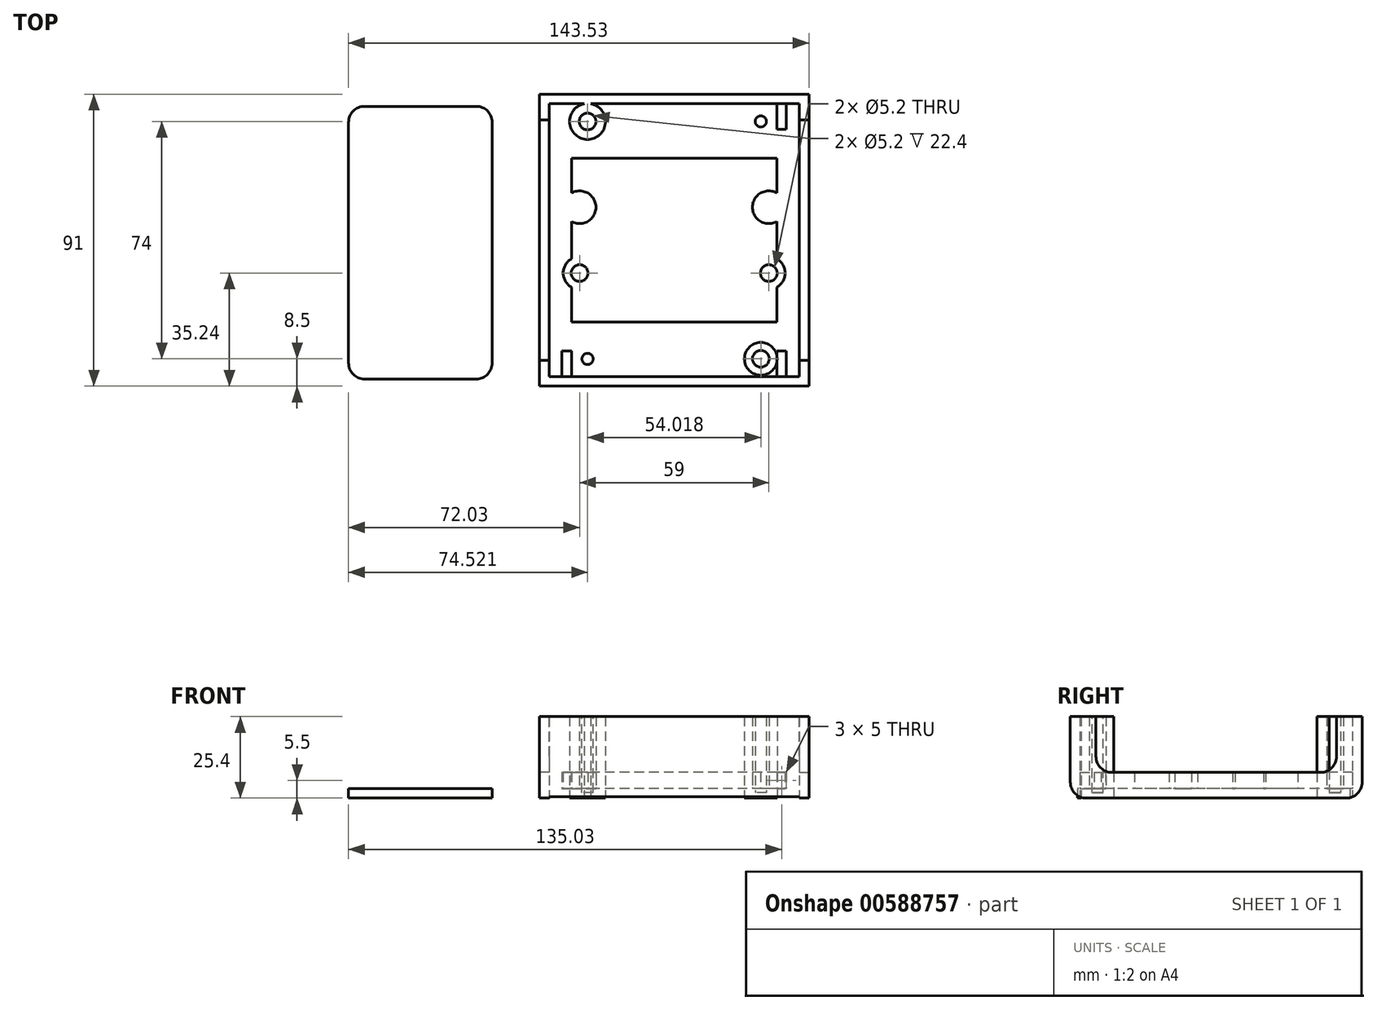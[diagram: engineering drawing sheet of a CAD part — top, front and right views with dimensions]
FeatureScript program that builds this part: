
annotation { "Feature Type Name" : "Feature", "Feature Type Description" : "" }
export const myFeature = defineFeature(function(context is Context, id is Id, definition is map)
    precondition{}
    {
        {
            assignVariable(context, id + "F0", {"name" : "hull_thickness", "anyValue" : 3});
        }
        {
            assignVariable(context, id + "F1", {"name" : "height", "anyValue" : 25.4});
        }
        {
            var Q0;
            Q0=qCreatedBy(makeId("Top.planeOp"),FACE);
            var sketch = newSketch(context, id + "F2", { "sketchPlane" : qUnion([Q0])});
            skLineSegment(sketch, "E0.bottom", {"start": v(42, 45.5) * mm, "end": v(-42, 45.5) * mm});
            skLineSegment(sketch, "E0.top", {"start": v(42, -45.5) * mm, "end": v(-42, -45.5) * mm});
            skLineSegment(sketch, "E0.left", {"start": v(42, 45.5) * mm, "end": v(42, -45.5) * mm});
            skLineSegment(sketch, "E0.right", {"start": v(-42, 45.5) * mm, "end": v(-42, -45.5) * mm});
            skPoint(sketch, "E0.middle", {"position": v(0, 0) * mm});
            skSolve(sketch);
        }
        {
            var Q0;
            Q0=makeQuery(id+"F2.imprint","IMPRINT",FACE,{"disambiguationData":[TD([[makeQuery(id+"F2.imprint","IMPRINT",EDGE,{"derivedFrom":sQuery(id+"F2.wireOp",EDGE,"E0.bottom")}),1.0]])]});
            extrude(context, id + "F3", {"entities" : qUnion([Q0]), "depth" : (getVariable(context, 'height')) * mm, "offsetDistance" : 25 * mm});
        }
        {
            var Q0;
            Q0=makeQuery(id+"F3.opExtrude","CAP_FACE",FACE,{"disambiguationData":[OSD([sQuery(id+"F2.wireOp",EDGE,"E0.bottom"),sQuery(id+"F2.wireOp",EDGE,"E0.top"),sQuery(id+"F2.wireOp",EDGE,"E0.left"),sQuery(id+"F2.wireOp",EDGE,"E0.right")])],"isStart":false});
            shell(context, id + "F4", {"entities" : qUnion([Q0]), "thickness" : (getVariable(context, 'hull_thickness')) * mm});
        }
        {
            var Q0;
            Q0=makeQuery(id+"F4.opShell","OFFSET_FACE",FACE,{"disambiguationData":[OSD([sQuery(id+"F2.wireOp",EDGE,"E0.bottom"),sQuery(id+"F2.wireOp",EDGE,"E0.top"),sQuery(id+"F2.wireOp",EDGE,"E0.left"),sQuery(id+"F2.wireOp",EDGE,"E0.right")])]});
            var sketch = newSketch(context, id + "F5", { "sketchPlane" : qUnion([Q0])});
            skLineSegment(sketch, "E1.bottom", {"start": v(42, 45.5) * mm, "end": v(-42, 45.5) * mm});
            skLineSegment(sketch, "E1.top", {"start": v(42, -45.5) * mm, "end": v(-42, -45.5) * mm});
            skLineSegment(sketch, "E1.left", {"start": v(42, 45.5) * mm, "end": v(42, -45.5) * mm});
            skLineSegment(sketch, "E1.right", {"start": v(-42, 45.5) * mm, "end": v(-42, -45.5) * mm});
            skPoint(sketch, "E1.middle", {"position": v(0, 0) * mm});
            skCircle(sketch, "E2", {"center": v(-27, 37) * mm, "radius": 2.6 * mm});
            skCircle(sketch, "E3.MirrorC", {"center": v(27, -37) * mm, "radius": 2.6 * mm});
            skCircle(sketch, "E4.MirrorC", {"center": v(27, 37) * mm, "radius": 1.75 * mm});
            skCircle(sketch, "E5.MirrorC", {"center": v(-27, -37) * mm, "radius": 1.75 * mm});
            skCircle(sketch, "E6", {"center": v(-27, 37) * mm, "radius": 5.6 * mm});
            skCircle(sketch, "E7", {"center": v(27, 37) * mm, "radius": 5.1 * mm});
            skCircle(sketch, "E8", {"center": v(27, -37) * mm, "radius": 5.1 * mm});
            skCircle(sketch, "E9", {"center": v(-27, -37) * mm, "radius": 5.1 * mm});
            skSolve(sketch);
        }
        {
            var Q0;
            Q0=makeQuery(id+"F5.imprint","IMPRINT",FACE,{"disambiguationData":[TD([[makeQuery(id+"F5.imprint","IMPRINT",EDGE,{"derivedFrom":sQuery(id+"F5.wireOp",EDGE,"E2")}),-1.0]])]});
            var Q1;
            Q1=makeQuery(id+"F5.imprint","IMPRINT",FACE,{"disambiguationData":[TD([[makeQuery(id+"F5.imprint","IMPRINT",EDGE,{"derivedFrom":sQuery(id+"F5.wireOp",EDGE,"E4.MirrorC")}),1.0]])]});
            var Q2;
            Q2=makeQuery(id+"F5.imprint","IMPRINT",FACE,{"disambiguationData":[TD([[makeQuery(id+"F5.imprint","IMPRINT",EDGE,{"derivedFrom":sQuery(id+"F5.wireOp",EDGE,"E5.MirrorC")}),1.0]])]});
            var Q3;
            Q3=makeQuery(id+"F5.imprint","IMPRINT",FACE,{"disambiguationData":[TD([[makeQuery(id+"F5.imprint","IMPRINT",EDGE,{"derivedFrom":sQuery(id+"F5.wireOp",EDGE,"E3.MirrorC")}),-1.0]])]});
            var Q4;
            Q4=makeQuery(id+"F3.opExtrude","CAP_FACE",FACE,{"disambiguationData":[OSD([sQuery(id+"F2.wireOp",EDGE,"E0.bottom"),sQuery(id+"F2.wireOp",EDGE,"E0.top"),sQuery(id+"F2.wireOp",EDGE,"E0.left"),sQuery(id+"F2.wireOp",EDGE,"E0.right")])],"isStart":false});
            extrude(context, id + "F6", {"entities" : qUnion([Q0, Q1, Q2, Q3]), "operationType" : NewBodyOperationType.ADD, "endBound" : BoundingType.UP_TO_SURFACE, "depth" : 25 * mm, "endBoundEntityFace" : qUnion([Q4]), "offsetDistance" : 25 * mm});
        }
        {
            var Q0;
            Q0=makeQuery(id+"F6.boolean.opBoolean","SPLIT",FACE,{"disambiguationData":[TD([makeQuery(id+"F6.opExtrude","SWEPT_FACE",FACE,{"disambiguationData":[OSD([sQuery(id+"F5.wireOp",EDGE,"E4.MirrorC")])]})])],"derivedFrom":makeQuery(id+"F4.opShell","OFFSET_FACE",FACE,{"disambiguationData":[OSD([sQuery(id+"F2.wireOp",EDGE,"E0.bottom"),sQuery(id+"F2.wireOp",EDGE,"E0.top"),sQuery(id+"F2.wireOp",EDGE,"E0.left"),sQuery(id+"F2.wireOp",EDGE,"E0.right")])]})});
            var Q1;
            Q1=makeQuery(id+"F6.boolean.opBoolean","SPLIT",FACE,{"disambiguationData":[TD([makeQuery(id+"F6.opExtrude","SWEPT_FACE",FACE,{"disambiguationData":[OSD([sQuery(id+"F5.wireOp",EDGE,"E5.MirrorC")])]})])],"derivedFrom":makeQuery(id+"F4.opShell","OFFSET_FACE",FACE,{"disambiguationData":[OSD([sQuery(id+"F2.wireOp",EDGE,"E0.bottom"),sQuery(id+"F2.wireOp",EDGE,"E0.top"),sQuery(id+"F2.wireOp",EDGE,"E0.left"),sQuery(id+"F2.wireOp",EDGE,"E0.right")])]})});
            extrude(context, id + "F7", {"entities" : qUnion([Q0, Q1]), "operationType" : NewBodyOperationType.REMOVE, "oppositeDirection" : true, "depth" : (getVariable(context, 'hull_thickness') + 2) * mm, "offsetDistance" : 25 * mm});
        }
        {
            var Q0;
            Q0=makeQuery(id+"F4.opShell","OFFSET_FACE",FACE,{"disambiguationData":[OSD([sQuery(id+"F2.wireOp",EDGE,"E0.bottom"),sQuery(id+"F2.wireOp",EDGE,"E0.top"),sQuery(id+"F2.wireOp",EDGE,"E0.left"),sQuery(id+"F2.wireOp",EDGE,"E0.right"),sQuery(id+"F2.wireOp",EDGE,"eL5Ql05H-nG85-WWal-oX3w-YHL8OOMjOhxp"),sQuery(id+"F2.wireOp",EDGE,"f290e64b-64e9-48c8-af58-a6b25b4c3f2f0.MirrorC"),sQuery(id+"F2.wireOp",EDGE,"e85a2d5f-414d-4ce5-af83-38743a2f01e40.MirrorC"),sQuery(id+"F2.wireOp",EDGE,"274bf30f-67d7-4a17-8dd5-418a9566e7f40.MirrorC")])]});
            var sketch = newSketch(context, id + "F8", { "sketchPlane" : qUnion([Q0])});
            skLineSegment(sketch, "E10.bottom", {"start": v(-35, 42.5) * mm, "end": v(-32, 42.5) * mm});
            skLineSegment(sketch, "E10.top", {"start": v(-35, 34.5) * mm, "end": v(-32, 34.5) * mm});
            skLineSegment(sketch, "E10.left", {"start": v(-35, 42.5) * mm, "end": v(-35, 34.5) * mm});
            skLineSegment(sketch, "E10.right", {"start": v(-32, 42.5) * mm, "end": v(-32, 34.5) * mm});
            skLineSegment(sketch, "E11.MirrorCS", {"start": v(35, 42.5) * mm, "end": v(35, 34.5) * mm});
            skLineSegment(sketch, "E12.MirrorCS", {"start": v(32, 42.5) * mm, "end": v(32, 34.5) * mm});
            skLineSegment(sketch, "E13.MirrorCS", {"start": v(35, 42.5) * mm, "end": v(32, 42.5) * mm});
            skLineSegment(sketch, "E14.MirrorCS", {"start": v(35, 34.5) * mm, "end": v(32, 34.5) * mm});
            skLineSegment(sketch, "E15.MirrorCS", {"start": v(-35, -42.5) * mm, "end": v(-35, -34.5) * mm});
            skLineSegment(sketch, "E16.MirrorCS", {"start": v(-32, -42.5) * mm, "end": v(-32, -34.5) * mm});
            skLineSegment(sketch, "E17.MirrorCS", {"start": v(-35, -42.5) * mm, "end": v(-32, -42.5) * mm});
            skLineSegment(sketch, "E18.MirrorCS", {"start": v(-35, -34.5) * mm, "end": v(-32, -34.5) * mm});
            skLineSegment(sketch, "E19.MirrorCS", {"start": v(35, -42.5) * mm, "end": v(32, -42.5) * mm});
            skLineSegment(sketch, "E20.MirrorCS", {"start": v(35, -42.5) * mm, "end": v(35, -34.5) * mm});
            skLineSegment(sketch, "E21.MirrorCS", {"start": v(32, -42.5) * mm, "end": v(32, -34.5) * mm});
            skLineSegment(sketch, "E22.MirrorCS", {"start": v(35, -34.5) * mm, "end": v(32, -34.5) * mm});
            skSolve(sketch);
        }
        {
            var Q0;
            Q0=makeQuery(id+"F8.imprint","IMPRINT",FACE,{"disambiguationData":[TD([[makeQuery(id+"F8.imprint","IMPRINT",EDGE,{"derivedFrom":sQuery(id+"F8.wireOp",EDGE,"E10.bottom")}),1.0]])]});
            var Q1;
            Q1=makeQuery(id+"F8.imprint","IMPRINT",FACE,{"disambiguationData":[TD([[makeQuery(id+"F8.imprint","IMPRINT",EDGE,{"derivedFrom":sQuery(id+"F8.wireOp",EDGE,"E11.MirrorCS")}),-1.0]])]});
            var Q2;
            Q2=makeQuery(id+"F8.imprint","IMPRINT",FACE,{"disambiguationData":[TD([[makeQuery(id+"F8.imprint","IMPRINT",EDGE,{"derivedFrom":sQuery(id+"F8.wireOp",EDGE,"E19.MirrorCS")}),-1.0]])]});
            var Q3;
            Q3=makeQuery(id+"F8.imprint","IMPRINT",FACE,{"disambiguationData":[TD([[makeQuery(id+"F8.imprint","IMPRINT",EDGE,{"derivedFrom":sQuery(id+"F8.wireOp",EDGE,"E15.MirrorCS")}),-1.0]])]});
            var Q4;
            Q4=makeQuery(id+"F8.imprint","IMPRINT",FACE,{"disambiguationData":[TD([[makeQuery(id+"F8.imprint","IMPRINT",EDGE,{"derivedFrom":sQuery(id+"F8.wireOp",EDGE,"E19.MirrorCS")}),1.0]])]});
            extrude(context, id + "F9", {"entities" : qUnion([Q0, Q1, Q2, Q3, Q4]), "operationType" : NewBodyOperationType.ADD, "depth" : 5 * mm, "offsetDistance" : 25 * mm});
        }
        {
            var Q0;
            {var subQ0=sQuery(id+"F2.wireOp",EDGE,"1cf9a666-e3d8-4fc7-9719-87b095cac5dd0.MirrorC");var subQ1=sQuery(id+"F2.wireOp",EDGE,"df13a3ce-5ca3-4fce-87e2-5a91c4b1ec740.MirrorC");var subQ2=sQuery(id+"F2.wireOp",EDGE,"274bf30f-67d7-4a17-8dd5-418a9566e7f40.MirrorC");var subQ3=sQuery(id+"F2.wireOp",EDGE,"JOWLscD1-6M25-fwtu-QNnx-YdRd9momwUJd");var subQ4=sQuery(id+"F2.wireOp",EDGE,"E0.right");var subQ5=sQuery(id+"F2.wireOp",EDGE,"E0.left");var subQ6=sQuery(id+"F2.wireOp",EDGE,"E0.top");var subQ7=sQuery(id+"F2.wireOp",EDGE,"E0.bottom");Q0=makeQuery(id+"F4.opShell","OFFSET_FACE",FACE,{"disambiguationData":[OSD([subQ7,subQ6,subQ5,subQ4,subQ3,subQ2,subQ1,subQ0]),TDD([makeQuery(id+"F3.opExtrude","CAP_FACE",FACE,{"disambiguationData":[OSD([subQ7,subQ6,subQ5,subQ4,subQ3,subQ2,subQ1,subQ0])],"isStart":true})])]});}
            var sketch = newSketch(context, id + "F10", { "sketchPlane" : qUnion([Q0])});
            skLineSegment(sketch, "E23.bottom", {"start": v(32, 25.5) * mm, "end": v(-32, 25.5) * mm});
            skLineSegment(sketch, "E23.top", {"start": v(32, -25.5) * mm, "end": v(-32, -25.5) * mm});
            skLineSegment(sketch, "E23.left", {"start": v(32, 25.5) * mm, "end": v(32, -25.5) * mm});
            skLineSegment(sketch, "E23.right", {"start": v(-32, 25.5) * mm, "end": v(-32, -25.5) * mm});
            skPoint(sketch, "E23.middle", {"position": v(0, 0) * mm});
            skCircle(sketch, "E24", {"center": v(-29.5, -10.26) * mm, "radius": 2.6 * mm});
            skCircle(sketch, "E25.MirrorC", {"center": v(29.5, -10.26) * mm, "radius": 2.6 * mm});
            skCircle(sketch, "E26.MirrorC", {"center": v(-29.5, 10.26) * mm, "radius": 2.6 * mm});
            skCircle(sketch, "E27.MirrorC", {"center": v(29.5, 10.26) * mm, "radius": 2.6 * mm});
            skCircle(sketch, "E28", {"center": v(-29.5, -10.26) * mm, "radius": 5.1 * mm});
            skCircle(sketch, "E29.MirrorC", {"center": v(-29.5, 10.26) * mm, "radius": 5.1 * mm});
            skCircle(sketch, "E30.MirrorC", {"center": v(29.5, 10.26) * mm, "radius": 5.1 * mm});
            skCircle(sketch, "E31.MirrorC", {"center": v(29.5, -10.26) * mm, "radius": 5.1 * mm});
            skSolve(sketch);
        }
        {
            var Q0;
            {var subQ0=sQuery(id+"F10.wireOp",EDGE,"E29.MirrorC");var subQ1=sQuery(id+"F10.wireOp",EDGE,"E23.right");var subQ2=makeQuery(id+"F10.imprint","INTERSECT",VERTEX,{"disambiguationData":[OD(0.0)],"derivedFrom":[subQ1,subQ0]});Q0=makeQuery(id+"F10.imprint","IMPRINT",FACE,{"disambiguationData":[TD([[makeQuery(id+"F10.imprint","IMPRINT",EDGE,{"disambiguationData":[TD([[subQ2,-1.0]])],"derivedFrom":subQ1}),-1.0]])]});}
            var Q1;
            {var subQ0=sQuery(id+"F10.wireOp",EDGE,"E29.MirrorC");var subQ1=sQuery(id+"F10.wireOp",EDGE,"E23.right");var subQ2=makeQuery(id+"F10.imprint","INTERSECT",VERTEX,{"disambiguationData":[OD(0.0)],"derivedFrom":[subQ1,subQ0]});Q1=makeQuery(id+"F10.imprint","IMPRINT",FACE,{"disambiguationData":[TD([[makeQuery(id+"F10.imprint","IMPRINT",EDGE,{"disambiguationData":[TD([[subQ2,-1.0]])],"derivedFrom":subQ1}),1.0]])]});}
            var Q2;
            {var subQ0=sQuery(id+"F10.wireOp",EDGE,"E30.MirrorC");var subQ1=sQuery(id+"F10.wireOp",EDGE,"E23.left");var subQ2=makeQuery(id+"F10.imprint","INTERSECT",VERTEX,{"disambiguationData":[OD(0.0)],"derivedFrom":[subQ1,subQ0]});Q2=makeQuery(id+"F10.imprint","IMPRINT",FACE,{"disambiguationData":[TD([[makeQuery(id+"F10.imprint","IMPRINT",EDGE,{"disambiguationData":[TD([[subQ2,-1.0]])],"derivedFrom":subQ1}),-1.0]])]});}
            var Q3;
            {var subQ0=sQuery(id+"F10.wireOp",EDGE,"E30.MirrorC");var subQ1=sQuery(id+"F10.wireOp",EDGE,"E23.left");var subQ2=makeQuery(id+"F10.imprint","INTERSECT",VERTEX,{"disambiguationData":[OD(0.0)],"derivedFrom":[subQ1,subQ0]});Q3=makeQuery(id+"F10.imprint","IMPRINT",FACE,{"disambiguationData":[TD([[makeQuery(id+"F10.imprint","IMPRINT",EDGE,{"disambiguationData":[TD([[subQ2,-1.0]])],"derivedFrom":subQ1}),1.0]])]});}
            var Q4;
            {var subQ0=sQuery(id+"F10.wireOp",EDGE,"E31.MirrorC");var subQ1=sQuery(id+"F10.wireOp",EDGE,"E23.left");var subQ2=makeQuery(id+"F10.imprint","INTERSECT",VERTEX,{"disambiguationData":[OD(0.0)],"derivedFrom":[subQ1,subQ0]});Q4=makeQuery(id+"F10.imprint","IMPRINT",FACE,{"disambiguationData":[TD([[makeQuery(id+"F10.imprint","IMPRINT",EDGE,{"disambiguationData":[TD([[subQ2,-1.0]])],"derivedFrom":subQ1}),-1.0]])]});}
            var Q5;
            {var subQ0=sQuery(id+"F10.wireOp",EDGE,"E31.MirrorC");var subQ1=sQuery(id+"F10.wireOp",EDGE,"E23.left");var subQ2=makeQuery(id+"F10.imprint","INTERSECT",VERTEX,{"disambiguationData":[OD(0.0)],"derivedFrom":[subQ1,subQ0]});Q5=makeQuery(id+"F10.imprint","IMPRINT",FACE,{"disambiguationData":[TD([[makeQuery(id+"F10.imprint","IMPRINT",EDGE,{"disambiguationData":[TD([[subQ2,-1.0]])],"derivedFrom":subQ1}),1.0]])]});}
            var Q6;
            {var subQ0=sQuery(id+"F10.wireOp",EDGE,"E28");var subQ1=sQuery(id+"F10.wireOp",EDGE,"E23.right");var subQ2=makeQuery(id+"F10.imprint","INTERSECT",VERTEX,{"disambiguationData":[OD(0.0)],"derivedFrom":[subQ1,subQ0]});Q6=makeQuery(id+"F10.imprint","IMPRINT",FACE,{"disambiguationData":[TD([[makeQuery(id+"F10.imprint","IMPRINT",EDGE,{"disambiguationData":[TD([[subQ2,-1.0]])],"derivedFrom":subQ1}),-1.0]])]});}
            var Q7;
            {var subQ0=sQuery(id+"F10.wireOp",EDGE,"E28");var subQ1=sQuery(id+"F10.wireOp",EDGE,"E23.right");var subQ2=makeQuery(id+"F10.imprint","INTERSECT",VERTEX,{"disambiguationData":[OD(0.0)],"derivedFrom":[subQ1,subQ0]});Q7=makeQuery(id+"F10.imprint","IMPRINT",FACE,{"disambiguationData":[TD([[makeQuery(id+"F10.imprint","IMPRINT",EDGE,{"disambiguationData":[TD([[subQ2,-1.0]])],"derivedFrom":subQ1}),1.0]])]});}
            extrude(context, id + "F11", {"entities" : qUnion([Q0, Q1, Q2, Q3, Q4, Q5, Q6, Q7]), "operationType" : NewBodyOperationType.ADD, "depth" : 5 * mm, "offsetDistance" : 25 * mm});
        }
        {
            assignVariable(context, id + "F12", {"name" : "countersink_depth", "anyValue" : 1.7});
        }
        {
            var Q0;
            Q0=makeQuery(id+"F2.imprint","IMPRINT",FACE,{"disambiguationData":[TD([[makeQuery(id+"F2.imprint","IMPRINT",EDGE,{"derivedFrom":sQuery(id+"F2.wireOp",EDGE,"E0.bottom")}),1.0]])]});
            var sketch = newSketch(context, id + "F13", { "sketchPlane" : qUnion([Q0])});
            skCircle(sketch, "E32", {"center": v(-27, -37) * mm, "radius": 3 * mm});
            skCircle(sketch, "E33", {"center": v(27, 37) * mm, "radius": 3 * mm});
            skSolve(sketch);
        }
        {
            var Q0;
            Q0 = qSketchRegion(id + "F13", true);
            extrude(context, id + "F14", {"entities" : qUnion([Q0]), "operationType" : NewBodyOperationType.REMOVE, "depth" : (getVariable(context, 'countersink_depth')) * mm, "offsetDistance" : 25 * mm});
        }
        {
            var Q0;
            Q0=makeQuery(id+"F3.opExtrude","CAP_EDGE",EDGE,{"disambiguationData":[OSD([sQuery(id+"F2.wireOp",EDGE,"E0.top")])],"isStart":true});
            var Q1;
            Q1=makeQuery(id+"F3.opExtrude","CAP_EDGE",EDGE,{"disambiguationData":[OSD([sQuery(id+"F2.wireOp",EDGE,"E0.bottom")])],"isStart":true});
            fillet(context, id + "F15", {"entities" : qUnion([Q0, Q1]), "radius" : 5 * mm, "tangentPropagation" : true, "allowEdgeOverflow" : false});
        }
        {
            var Q0;
            Q0=makeQuery(id+"F3.opExtrude","SWEPT_FACE",FACE,{"disambiguationData":[OSD([sQuery(id+"F2.wireOp",EDGE,"E0.right")])]});
            var sketch = newSketch(context, id + "F16", { "sketchPlane" : qUnion([Q0])});
            skLineSegment(sketch, "E34.bottom", {"start": v(32.5, 8) * mm, "end": v(-32.5, 8) * mm});
            skLineSegment(sketch, "E34.top", {"start": v(37.5, 25.4) * mm, "end": v(-37.5, 25.4) * mm});
            skLineSegment(sketch, "E34.left", {"start": v(37.5, 13) * mm, "end": v(37.5, 25.4) * mm});
            skLineSegment(sketch, "E34.right", {"start": v(-37.5, 13) * mm, "end": v(-37.5, 25.4) * mm});
            skPoint(sketch, "E35.visualSharp", {"position": v(37.5, 8) * mm});
            skArc(sketch, "E35.filletArc", {"start": v(32.5, 8) * mm, "mid": v(36.04, 9.46) * mm, "end": v(37.5, 13) * mm});
            skPoint(sketch, "E36.visualSharp", {"position": v(-37.5, 8) * mm});
            skArc(sketch, "E36.filletArc", {"start": v(-37.5, 13) * mm, "mid": v(-36.04, 9.46) * mm, "end": v(-32.5, 8) * mm});
            skSolve(sketch);
        }
        {
            var Q0;
            Q0=makeQuery(id+"F16.imprint","IMPRINT",FACE,{"disambiguationData":[TD([[makeQuery(id+"F16.imprint","IMPRINT",EDGE,{"derivedFrom":sQuery(id+"F16.wireOp",EDGE,"E34.bottom")}),-1.0]])]});
            extrude(context, id + "F17", {"entities" : qUnion([Q0]), "operationType" : NewBodyOperationType.REMOVE, "oppositeDirection" : true, "depth" : (getVariable(context, 'hull_thickness')) * mm, "offsetDistance" : 25 * mm});
        }
        {
            var Q0;
            Q0=makeQuery(id+"F3.opExtrude","SWEPT_FACE",FACE,{"disambiguationData":[OSD([sQuery(id+"F2.wireOp",EDGE,"E0.left")])]});
            var sketch = newSketch(context, id + "F18", { "sketchPlane" : qUnion([Q0])});
            skLineSegment(sketch, "E37.bottom", {"start": v(-37.5, 25.4) * mm, "end": v(37.5, 25.4) * mm});
            skLineSegment(sketch, "E37.top", {"start": v(32.5, 8) * mm, "end": v(-32.5, 8) * mm});
            skLineSegment(sketch, "E37.left", {"start": v(37.5, 13) * mm, "end": v(37.5, 25.4) * mm});
            skLineSegment(sketch, "E37.right", {"start": v(-37.5, 13) * mm, "end": v(-37.5, 25.4) * mm});
            skPoint(sketch, "E38.visualSharp", {"position": v(-37.5, 8) * mm});
            skArc(sketch, "E38.filletArc", {"start": v(-37.5, 13) * mm, "mid": v(-36.04, 9.46) * mm, "end": v(-32.5, 8) * mm});
            skPoint(sketch, "E39.visualSharp", {"position": v(37.5, 8) * mm});
            skArc(sketch, "E39.filletArc", {"start": v(32.5, 8) * mm, "mid": v(36.04, 9.46) * mm, "end": v(37.5, 13) * mm});
            skSolve(sketch);
        }
        {
            var Q0;
            Q0=makeQuery(id+"F18.imprint","IMPRINT",FACE,{"disambiguationData":[TD([[makeQuery(id+"F18.imprint","IMPRINT",EDGE,{"derivedFrom":sQuery(id+"F18.wireOp",EDGE,"E37.bottom")}),1.0]])]});
            extrude(context, id + "F19", {"entities" : qUnion([Q0]), "operationType" : NewBodyOperationType.REMOVE, "oppositeDirection" : true, "depth" : (getVariable(context, 'hull_thickness')) * mm, "offsetDistance" : 25 * mm});
        }
        {
            var Q0;
            Q0=makeQuery(id+"F2.imprint","IMPRINT",FACE,{"disambiguationData":[TD([[makeQuery(id+"F2.imprint","IMPRINT",EDGE,{"derivedFrom":sQuery(id+"F2.wireOp",EDGE,"E0.bottom")}),1.0]])]});
            var sketch = newSketch(context, id + "F20", { "sketchPlane" : qUnion([Q0])});
            skLineSegment(sketch, "E40.bottom", {"start": v(-13.75, 25.5) * mm, "end": v(-10.75, 25.5) * mm});
            skLineSegment(sketch, "E40.top", {"start": v(-13.75, -25.5) * mm, "end": v(-10.75, -25.5) * mm});
            skLineSegment(sketch, "E40.left", {"start": v(-13.75, 25.5) * mm, "end": v(-13.75, -25.5) * mm});
            skLineSegment(sketch, "E40.right", {"start": v(-10.75, 25.5) * mm, "end": v(-10.75, -25.5) * mm});
            skLineSegment(sketch, "E41.1.0.0", {"start": v(-5.75, 25.5) * mm, "end": v(-5.75, -25.5) * mm});
            skLineSegment(sketch, "E41.1.0.1", {"start": v(-8.75, 25.5) * mm, "end": v(-8.75, -25.5) * mm});
            skLineSegment(sketch, "E41.1.0.2", {"start": v(-8.75, -25.5) * mm, "end": v(-5.75, -25.5) * mm});
            skLineSegment(sketch, "E41.1.0.3", {"start": v(-8.75, 25.5) * mm, "end": v(-5.75, 25.5) * mm});
            skLineSegment(sketch, "E41.2.0.0", {"start": v(-0.75, 25.5) * mm, "end": v(-0.75, -25.5) * mm});
            skLineSegment(sketch, "E41.2.0.1", {"start": v(-3.75, 25.5) * mm, "end": v(-3.75, -25.5) * mm});
            skLineSegment(sketch, "E41.2.0.2", {"start": v(-3.75, -25.5) * mm, "end": v(-0.75, -25.5) * mm});
            skLineSegment(sketch, "E41.2.0.3", {"start": v(-3.75, 25.5) * mm, "end": v(-0.75, 25.5) * mm});
            skLineSegment(sketch, "E41.3.0.0", {"start": v(4.25, 25.5) * mm, "end": v(4.25, -25.5) * mm});
            skLineSegment(sketch, "E41.3.0.1", {"start": v(1.25, 25.5) * mm, "end": v(1.25, -25.5) * mm});
            skLineSegment(sketch, "E41.3.0.2", {"start": v(1.25, -25.5) * mm, "end": v(4.25, -25.5) * mm});
            skLineSegment(sketch, "E41.3.0.3", {"start": v(1.25, 25.5) * mm, "end": v(4.25, 25.5) * mm});
            skLineSegment(sketch, "E41.4.0.0", {"start": v(9.25, 25.5) * mm, "end": v(9.25, -25.5) * mm});
            skLineSegment(sketch, "E41.4.0.1", {"start": v(6.25, 25.5) * mm, "end": v(6.25, -25.5) * mm});
            skLineSegment(sketch, "E41.4.0.2", {"start": v(6.25, -25.5) * mm, "end": v(9.25, -25.5) * mm});
            skLineSegment(sketch, "E41.4.0.3", {"start": v(6.25, 25.5) * mm, "end": v(9.25, 25.5) * mm});
            skLineSegment(sketch, "E41.5.0.0", {"start": v(14.25, 25.5) * mm, "end": v(14.25, -25.5) * mm});
            skLineSegment(sketch, "E41.5.0.1", {"start": v(11.25, 25.5) * mm, "end": v(11.25, -25.5) * mm});
            skLineSegment(sketch, "E41.5.0.2", {"start": v(11.25, -25.5) * mm, "end": v(14.25, -25.5) * mm});
            skLineSegment(sketch, "E41.5.0.3", {"start": v(11.25, 25.5) * mm, "end": v(14.25, 25.5) * mm});
            skLineSegment(sketch, "E41.direction1", {"start": v(-13.75, -25.5) * mm, "end": v(-8.75, -25.5) * mm, "construction": true});
            skSolve(sketch);
        }
        {
            var Q0;
            Q0 = qSketchRegion(id + "F20", true);
            extrude(context, id + "F21", {"entities" : qUnion([Q0]), "operationType" : NewBodyOperationType.REMOVE, "depth" : (getVariable(context, 'hull_thickness')) * mm, "offsetDistance" : 25 * mm});
        }
        {
            var Q0;
            Q0=qCreatedBy(makeId("Top.planeOp"),FACE);
            var sketch = newSketch(context, id + "F22", { "sketchPlane" : qUnion([Q0])});
            skLineSegment(sketch, "E42.bottom", {"start": v(-61.73, 41.73) * mm, "end": v(-96.53, 41.73) * mm});
            skLineSegment(sketch, "E42.top", {"start": v(-61.73, -43.27) * mm, "end": v(-96.53, -43.27) * mm});
            skLineSegment(sketch, "E42.left", {"start": v(-56.73, 36.73) * mm, "end": v(-56.73, -38.27) * mm});
            skLineSegment(sketch, "E42.right", {"start": v(-101.53, 36.73) * mm, "end": v(-101.53, -38.27) * mm});
            skPoint(sketch, "E43.visualSharp", {"position": v(-56.73, 41.73) * mm});
            skArc(sketch, "E43.filletArc", {"start": v(-56.73, 36.73) * mm, "mid": v(-58.2, 40.27) * mm, "end": v(-61.73, 41.73) * mm});
            skPoint(sketch, "E44.visualSharp", {"position": v(-101.53, 41.73) * mm});
            skArc(sketch, "E44.filletArc", {"start": v(-96.53, 41.73) * mm, "mid": v(-100.07, 40.27) * mm, "end": v(-101.53, 36.73) * mm});
            skPoint(sketch, "E45.visualSharp", {"position": v(-101.53, -43.27) * mm});
            skArc(sketch, "E45.filletArc", {"start": v(-101.53, -38.27) * mm, "mid": v(-100.07, -41.8) * mm, "end": v(-96.53, -43.27) * mm});
            skPoint(sketch, "E46.visualSharp", {"position": v(-56.73, -43.27) * mm});
            skArc(sketch, "E46.filletArc", {"start": v(-61.73, -43.27) * mm, "mid": v(-58.2, -41.8) * mm, "end": v(-56.73, -38.27) * mm});
            skSolve(sketch);
        }
        {
            var Q0;
            Q0 = qSketchRegion(id + "F22", true);
            extrude(context, id + "F23", {"entities" : qUnion([Q0]), "depth" : (getVariable(context, 'hull_thickness')) * mm, "offsetDistance" : 25 * mm});
        }
    });
